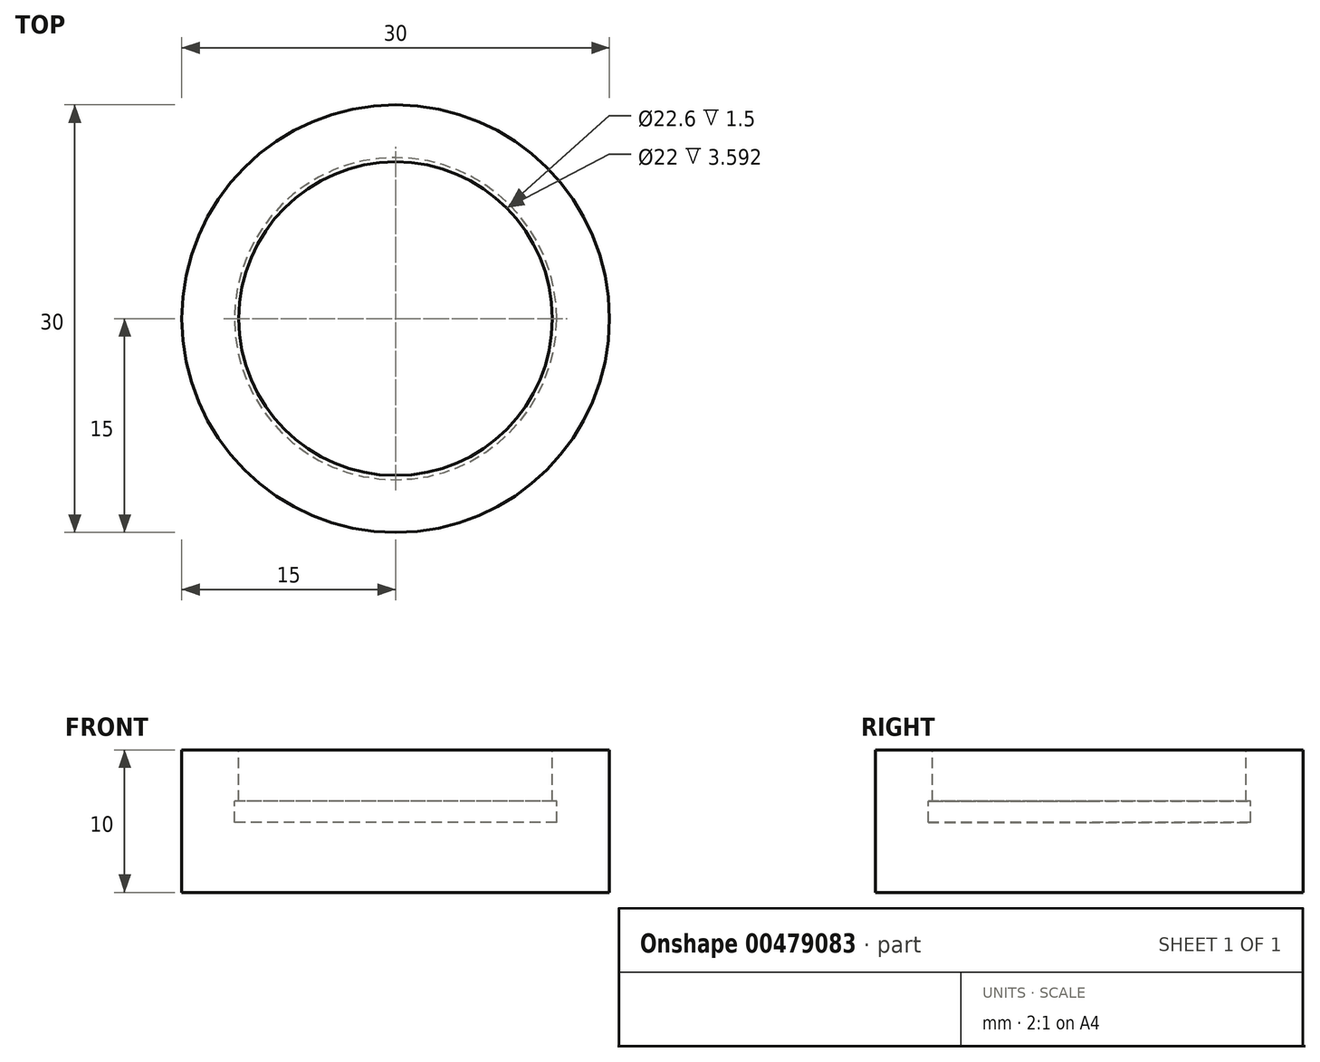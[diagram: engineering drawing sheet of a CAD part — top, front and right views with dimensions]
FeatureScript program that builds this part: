
annotation { "Feature Type Name" : "Feature", "Feature Type Description" : "" }
export const myFeature = defineFeature(function(context is Context, id is Id, definition is map)
    precondition{}
    {
        {
            var Q0;
            Q0=qCreatedBy(makeId("Front.planeOp"),FACE);
            var sketch = newSketch(context, id + "F0", { "sketchPlane" : qUnion([Q0])});
            skLineSegment(sketch, "E0", {"start": v(0, 0) * mm, "end": v(-15, 0) * mm});
            skLineSegment(sketch, "E1", {"start": v(-15, 0) * mm, "end": v(-15, 10) * mm});
            skLineSegment(sketch, "E2", {"start": v(-15, 10) * mm, "end": v(-11, 10) * mm});
            skLineSegment(sketch, "E3", {"start": v(-11, 10) * mm, "end": v(-11, 6.4) * mm});
            skLineSegment(sketch, "E4", {"start": v(-11, 6.4) * mm, "end": v(-11.3, 6.4) * mm});
            skLineSegment(sketch, "E5", {"start": v(-11.3, 6.4) * mm, "end": v(-11.3, 4.9) * mm});
            skLineSegment(sketch, "E6", {"start": v(-11.3, 4.9) * mm, "end": v(0, 4.9) * mm});
            skLineSegment(sketch, "E7", {"start": v(0, 4.9) * mm, "end": v(0, 0) * mm});
            skSolve(sketch);
        }
        {
            var Q0;
            Q0=makeQuery(id+"F0.imprint","IMPRINT",FACE,{"disambiguationData":[TD([[makeQuery(id+"F0.imprint","IMPRINT",EDGE,{"derivedFrom":sQuery(id+"F0.wireOp",EDGE,"E0")}),-1.0]])]});
            var Q1;
            Q1=sQuery(id+"F0.wireOp",EDGE,"E7");
            revolve(context, id + "F1", {"entities" : qUnion([Q0]), "axis" : qUnion([Q1]), "revolveType" : RevolveType.FULL});
        }
    });
